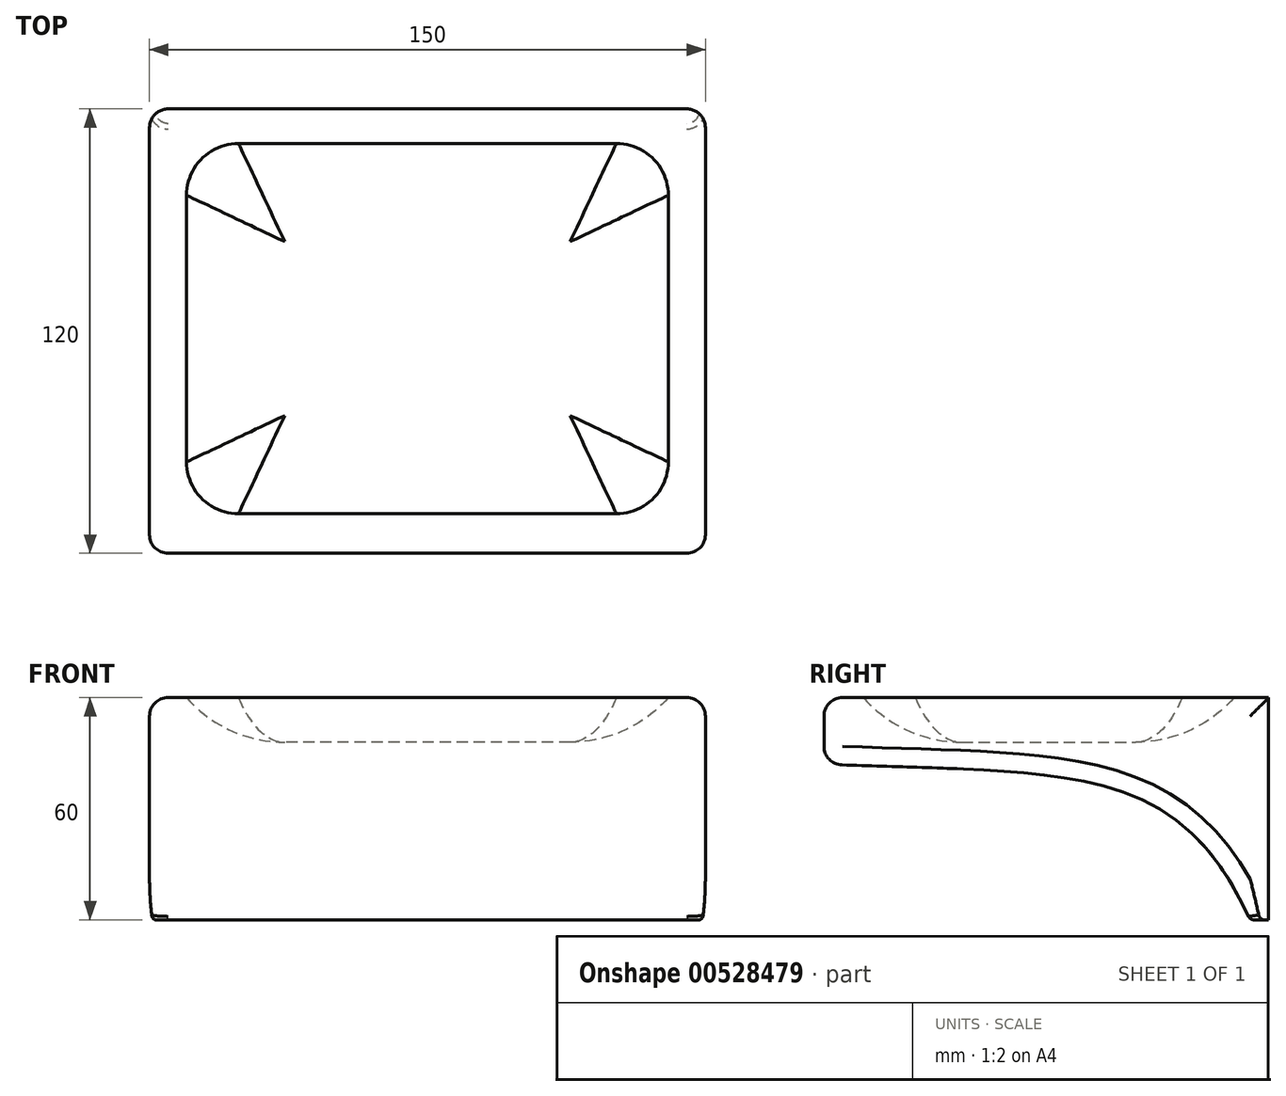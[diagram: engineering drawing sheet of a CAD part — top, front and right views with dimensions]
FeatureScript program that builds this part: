
annotation { "Feature Type Name" : "Feature", "Feature Type Description" : "" }
export const myFeature = defineFeature(function(context is Context, id is Id, definition is map)
    precondition{}
    {
        {
            var Q0;
            Q0=qCreatedBy(makeId("Right.planeOp"),FACE);
            var sketch = newSketch(context, id + "F0", { "sketchPlane" : qUnion([Q0])});
            skLineSegment(sketch, "E0", {"start": v(55.36, -20) * mm, "end": v(60.36, -20) * mm});
            skLineSegment(sketch, "E1", {"start": v(60.36, -20) * mm, "end": v(60.36, 40) * mm});
            skLineSegment(sketch, "E2", {"start": v(60.36, 40) * mm, "end": v(-59.64, 40) * mm});
            skLineSegment(sketch, "E3", {"start": v(-59.64, 40) * mm, "end": v(-59.64, 22) * mm});
            skFitSpline(sketch, "E4", {"points": [v(-59.64, 22) * mm, v(55.36, -20) * mm], "startDerivative": vector(201.84, -7.32) * mm, "endDerivative": vector(58.62, -128.53) * mm});
            skSolve(sketch);
        }
        {
            var Q0;
            Q0=makeQuery(id+"F0.imprint","IMPRINT",FACE,{"disambiguationData":[TD([[makeQuery(id+"F0.imprint","IMPRINT",EDGE,{"derivedFrom":sQuery(id+"F0.wireOp",EDGE,"E0")}),1.0]])]});
            extrude(context, id + "F1", {"entities" : qUnion([Q0]), "endBound" : BoundingType.SYMMETRIC, "depth" : 150 * mm, "offsetDistance" : 25 * mm});
        }
        {
            var Q0;
            Q0=makeQuery(id+"F1.opExtrude","SWEPT_EDGE",EDGE,{"disambiguationData":[OSD([sQuery(id+"F0.wireOp",EDGE,"E3"),sQuery(id+"F0.wireOp",EDGE,"U8TW26UN-RZ07-0nZT-lysD-zoQkEwGNOYQ5")])]});
            var Q1;
            Q1=makeQuery(id+"F1.opExtrude","SWEPT_EDGE",EDGE,{"disambiguationData":[OSD([sQuery(id+"F0.wireOp",EDGE,"E2"),sQuery(id+"F0.wireOp",EDGE,"E3")])]});
            fillet(context, id + "F2", {"entities" : qUnion([Q0, Q1]), "radius" : 5 * mm, "tangentPropagation" : true, "allowEdgeOverflow" : false});
        }
        {
            var Q0;
            Q0=makeQuery(id+"F1.opExtrude","CAP_FACE",FACE,{"disambiguationData":[OSD([sQuery(id+"F0.wireOp",EDGE,"E0"),sQuery(id+"F0.wireOp",EDGE,"E1"),sQuery(id+"F0.wireOp",EDGE,"E2"),sQuery(id+"F0.wireOp",EDGE,"E3"),sQuery(id+"F0.wireOp",EDGE,"U8TW26UN-RZ07-0nZT-lysD-zoQkEwGNOYQ5"),sQuery(id+"F0.wireOp",EDGE,"lEO603tg-e8Y2-3sv2-ZowU-qD5Z2dU0eWy5")])],"isStart":false});
            var Q1;
            Q1=makeQuery(id+"F1.opExtrude","CAP_FACE",FACE,{"disambiguationData":[OSD([sQuery(id+"F0.wireOp",EDGE,"E0"),sQuery(id+"F0.wireOp",EDGE,"E1"),sQuery(id+"F0.wireOp",EDGE,"E2"),sQuery(id+"F0.wireOp",EDGE,"E3"),sQuery(id+"F0.wireOp",EDGE,"U8TW26UN-RZ07-0nZT-lysD-zoQkEwGNOYQ5"),sQuery(id+"F0.wireOp",EDGE,"lEO603tg-e8Y2-3sv2-ZowU-qD5Z2dU0eWy5")])],"isStart":true});
            fillet(context, id + "F3", {"entities" : qUnion([Q0, Q1]), "radius" : 5 * mm, "tangentPropagation" : true, "allowEdgeOverflow" : false});
        }
        {
            var Q0;
            Q0=qCreatedBy(makeId("Right.planeOp"),FACE);
            var sketch = newSketch(context, id + "F4", { "sketchPlane" : qUnion([Q0])});
            skLineSegment(sketch, "E5", {"start": v(51.03, 40) * mm, "end": v(51.03, 28) * mm});
            skLineSegment(sketch, "E6", {"start": v(51.03, 28) * mm, "end": v(-48.97, 28) * mm});
            skLineSegment(sketch, "E7", {"start": v(-48.97, 28) * mm, "end": v(-48.97, 40) * mm});
            skLineSegment(sketch, "E8", {"start": v(-48.97, 40) * mm, "end": v(51.03, 40) * mm});
            skSolve(sketch);
        }
        {
            var Q0;
            Q0 = qSketchRegion(id + "F4", true);
            extrude(context, id + "F5", {"entities" : qUnion([Q0]), "operationType" : NewBodyOperationType.REMOVE, "endBound" : BoundingType.SYMMETRIC, "depth" : 130 * mm, "offsetDistance" : 25 * mm});
        }
        {
            var Q0;
            Q0=makeQuery(id+"F5.boolean.opBoolean","COPY",EDGE,{"derivedFrom":makeQuery(id+"F5.opExtrude","CAP_EDGE",EDGE,{"disambiguationData":[OSD([sQuery(id+"F4.wireOp",EDGE,"E5")])],"isStart":true})});
            var Q1;
            Q1=makeQuery(id+"F5.boolean.opBoolean","COPY",EDGE,{"derivedFrom":makeQuery(id+"F5.opExtrude","CAP_EDGE",EDGE,{"disambiguationData":[OSD([sQuery(id+"F4.wireOp",EDGE,"E5")])],"isStart":false})});
            var Q2;
            Q2=makeQuery(id+"F5.boolean.opBoolean","COPY",EDGE,{"derivedFrom":makeQuery(id+"F5.opExtrude","CAP_EDGE",EDGE,{"disambiguationData":[OSD([sQuery(id+"F4.wireOp",EDGE,"E7")])],"isStart":false})});
            var Q3;
            Q3=makeQuery(id+"F5.boolean.opBoolean","COPY",EDGE,{"derivedFrom":makeQuery(id+"F5.opExtrude","CAP_EDGE",EDGE,{"disambiguationData":[OSD([sQuery(id+"F4.wireOp",EDGE,"E7")])],"isStart":true})});
            fillet(context, id + "F6", {"entities" : qUnion([Q0, Q1, Q2, Q3]), "radius" : 14 * mm, "tangentPropagation" : true, "allowEdgeOverflow" : false});
        }
        {
            var Q0;
            Q0=makeQuery(id+"F5.boolean.opBoolean","COPY",FACE,{"derivedFrom":makeQuery(id+"F5.opExtrude","SWEPT_FACE",FACE,{"disambiguationData":[OSD([sQuery(id+"F4.wireOp",EDGE,"E6")])]})});
            fillet(context, id + "F7", {"entities" : qUnion([Q0]), "radius" : 35.25 * mm, "tangentPropagation" : true, "allowEdgeOverflow" : false});
        }
        {
            var Q0;
            Q0=makeQuery(id+"F1.opExtrude","SWEPT_EDGE",EDGE,{"disambiguationData":[OSD([sQuery(id+"F0.wireOp",EDGE,"E0"),sQuery(id+"F0.wireOp",EDGE,"E4")])]});
            fillet(context, id + "F8", {"entities" : qUnion([Q0]), "radius" : 1.59 * mm, "tangentPropagation" : true, "allowEdgeOverflow" : false});
        }
    });
